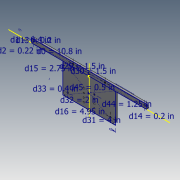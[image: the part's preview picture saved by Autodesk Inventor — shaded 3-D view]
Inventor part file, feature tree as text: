
AUTODESK INVENTOR PART (.ipt)
format: ipt  version: 2018.3 (Build 223284000, 284)  size: 149,504 bytes
history: native  units: in
note: dims shown in document units (in); Inventor stores cm internally (conversion verified against a paired STEP export)
features: hole x3, extrude x2, fillet x2, pattern_linear x1
ambient origin geometry x8: Origin, YZ Plane, XZ Plane, XY Plane, X Axis, Y Axis, Z Axis, Center Point
bodies: Solid1 (feature_tree)
feature tree (8):
  extrude  "Extrusion1"  Depth=10.8in
  hole  "Hole1"  [1 undecoded]
  fillet  "Fillet1"  Radius=0.22in
  extrude  "Extrusion2"  Depth=0.177in TaperAngle=0.0deg
  fillet  "Fillet2"  Radius=0.125in
  hole  "Hole2"  [1 undecoded]
  hole  "Hole3"  [1 undecoded]
  pattern_linear  "Rectangular Pattern1"  Spacing1=2.75in  [1 undecoded]
note: 4 required parameter values undecoded (feature->parameter linkage not recoverable at this tier; creation-order binding heuristic only, values carry confidence <= 0.55)
